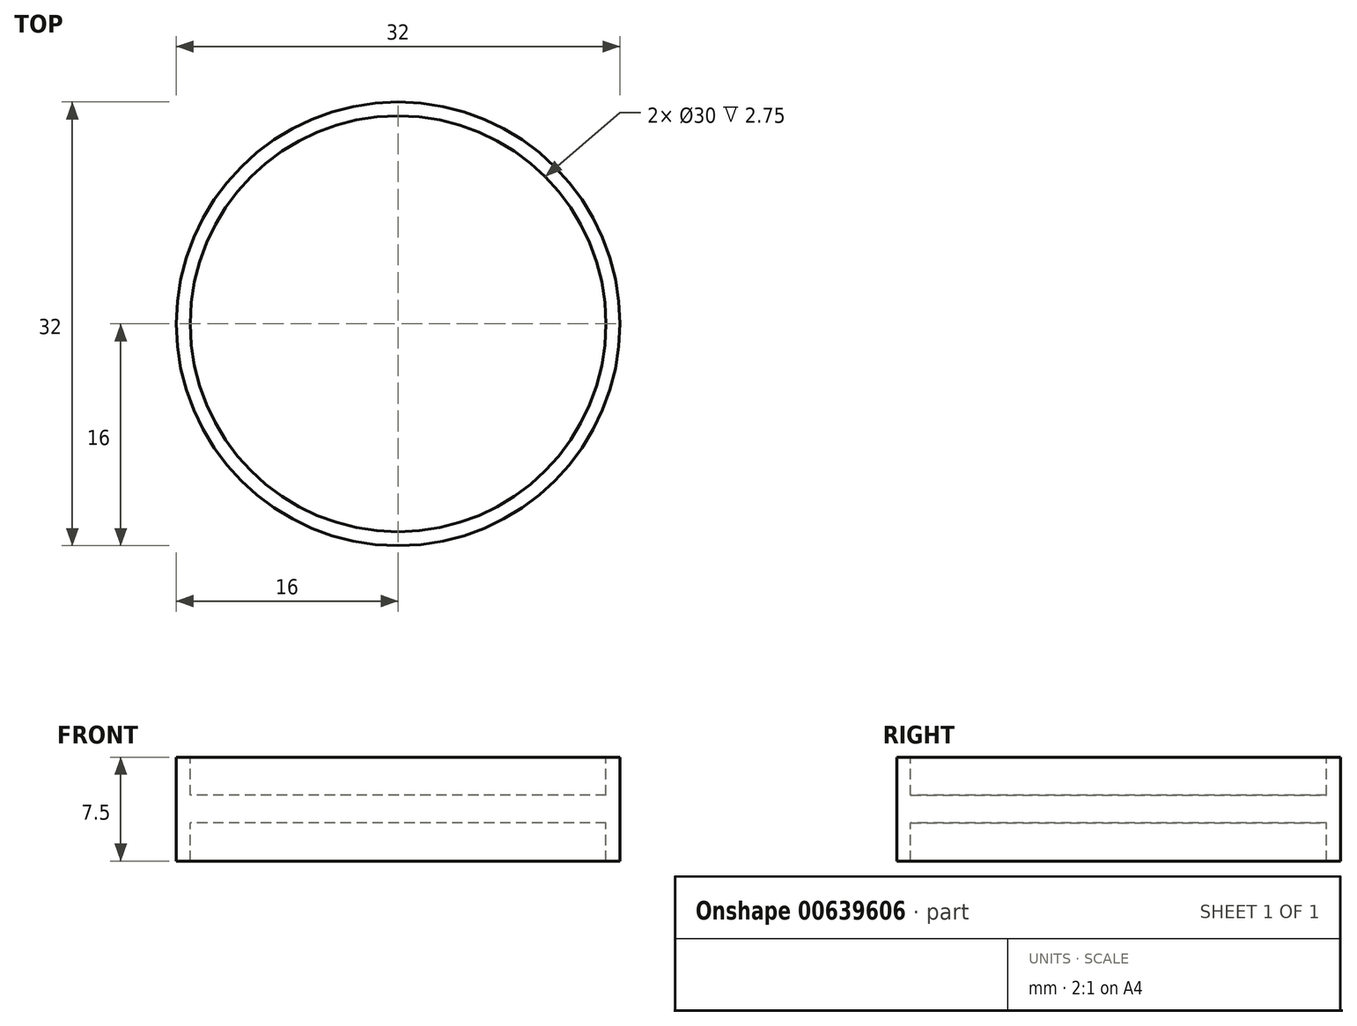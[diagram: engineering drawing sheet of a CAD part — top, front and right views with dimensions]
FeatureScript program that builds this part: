
annotation { "Feature Type Name" : "Feature", "Feature Type Description" : "" }
export const myFeature = defineFeature(function(context is Context, id is Id, definition is map)
    precondition{}
    {
        {
            var Q0;
            Q0=qCreatedBy(makeId("Front.planeOp"),FACE);
            var sketch = newSketch(context, id + "F0", { "sketchPlane" : qUnion([Q0])});
            skLineSegment(sketch, "E0", {"start": v(0, 1) * mm, "end": v(15, 1) * mm});
            skLineSegment(sketch, "E1", {"start": v(15, 1) * mm, "end": v(15, 3.75) * mm});
            skLineSegment(sketch, "E2", {"start": v(15, 3.75) * mm, "end": v(16, 3.75) * mm});
            skLineSegment(sketch, "E3", {"start": v(16, 3.75) * mm, "end": v(16, 0) * mm});
            skLineSegment(sketch, "E4.MirrorCS", {"start": v(16, -3.75) * mm, "end": v(16, 0) * mm});
            skLineSegment(sketch, "E5.MirrorCS", {"start": v(15, -3.75) * mm, "end": v(16, -3.75) * mm});
            skLineSegment(sketch, "E6.MirrorCS", {"start": v(15, -1) * mm, "end": v(15, -3.75) * mm});
            skLineSegment(sketch, "E7.MirrorCS", {"start": v(0, -1) * mm, "end": v(15, -1) * mm});
            skLineSegment(sketch, "E8", {"start": v(0, 1) * mm, "end": v(0, -1) * mm});
            skSolve(sketch);
        }
        {
            var Q0;
            Q0 = qSketchRegion(id + "F0", true);
            var Q1;
            Q1=sQuery(id+"F0.wireOp",EDGE,"E8");
            revolve(context, id + "F1", {"entities" : qUnion([Q0]), "axis" : qUnion([Q1]), "revolveType" : RevolveType.FULL});
        }
    });
